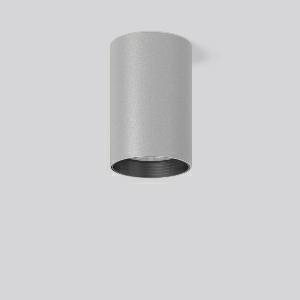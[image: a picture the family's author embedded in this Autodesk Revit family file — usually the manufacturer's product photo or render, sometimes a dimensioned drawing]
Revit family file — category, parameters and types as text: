
# Revit family: heledon_maxi_a_931222_004_3_98ae
name_source: partatom
category: Lighting Fixtures
units: mm (PartAtom-declared; Revit-internal decimal feet)

## family parameters
Cut with Voids When Loaded = No
Host = Face
Light Source = No
Part Type = Normal
Room Calculation Point = No
Round Connector Dimension = Use Diameter
Shared = No

## types (1)
- HELEDON maxi A (1 x LED Modul 935, 2850 lm, 3500)
    Apparent Load = 25 VA
    Approval mark = CE
    CIE Flux Codes = 96 100 100 100 100
    Color Rendering = 92
    Color Temperature = 3500
    Default Elevation = 1800 mm
    Description = Series: HELEDON maxi
Cylindrical surface-mounted downlight. Housing: die-cast aluminium, powder-coated. Internal ceiling frame polycarbonate with bayonet mounting. Black plastic ring and recessed LED to prevent glare from the side. Optical assembly with lens made of plastic (polycarbonate) for the best homogeneous light distribution - can be changed without tools. Best colour rendering index Ra>90. Suitable for Ceiling mounting. Easy installation with a separate ceiling frame with bayonet mounting and plug connection. Driver integrated. Connected via plug-in connector. High quality converter without flickering and stroboscopic effect. The following accessories can be mounted without use of tools: interchangeable lenses, decorative glasses, honeycomb louvre, clear and frosted diffusers, white interchangeable plastic ring. 
Colour: silver
Diameter: 123 mm
Height: 183 mm
Lamp: LED
Socket: without socket
Colour temperature: 3500K
Colour rendering index (CRI): 92
System power: 25 W
Rated luminous flux: 2850 lm
Luminous efficiency: 114 lm/W
Control gear: Regulated power supply
Protection class: I
Type of protection: IP 20
    Height = 183 mm
    Lamp = 1 x LED Modul 935
    Lamp Light Flux = 2850 lm
    Lamp count = 1
    Length = 123 mm
    Lifetime = 50000 h
    Luminous efficacy = 114 lm/W
    Manufacturer = RZB
    ModVariant = No
    Model = 931222.004.3
    Mounting Place = Ceiling
    Mounting Type = Surface mounted
    Number of Poles = 1
    OnlyDefault = Yes
    Power Factor = 1
    Product Name = HELEDON maxi A
    Product group = Surface mounted downlights
    ProductGroupID = 302
    Protection Class = Protection class I
    Protection Degree = IP 20
    RLX_Detail_Level = 1
    RLX_Emergency_Light_Flux = 0 lm
    RLX_Emergency_Type = 0
    RLX_Emergency_Type_DB = No
    RlxData = <blob elided: 99329 chars, md5=1286e1ed>
    Socket = socket
    Standby Power = 0 W
    System Light Flux = 2850 lm
    System Power = 25 W
    Type Comments = Product without accessories
    Type Image = 931193.004.jpg
    URL = http://relux.com
    VarID = ---
    Voltage = 230 V
    Voltage Range = 220-240 V
    Weight = 0.00 kg
    Width = 0 mm  [stored 0 ft]

note: [stored X ft] marks values corroborated as IEEE doubles in the binary element streams (Revit-internal decimal feet)

## geometry (parser evidence)
native form markers: Blend x4, Sweep x10
no freeform markers — native parametric forms only
